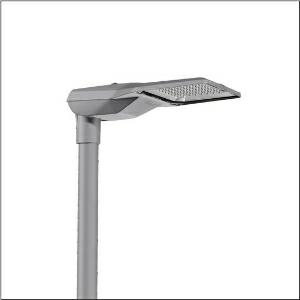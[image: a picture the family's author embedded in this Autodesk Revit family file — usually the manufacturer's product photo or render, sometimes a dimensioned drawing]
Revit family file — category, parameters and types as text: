
# Revit family: streetlight_sl_21_midi___p0_5a_5xe3v33s08nb_fb54
name_source: partatom
category: Lighting Fixtures
units: mm (PartAtom-declared; Revit-internal decimal feet)

## family parameters
Cut with Voids When Loaded = No
Host = Face
Light Source = No
Part Type = Normal
Room Calculation Point = No
Round Connector Dimension = Use Diameter
Shared = No

## types (1)
- --- (1 x LED, 22310 lm, 151.2 W, 3000K)
    Apparent Load = 151 VA
    CIE Flux Codes = 37 73 96 100 100
    Color Rendering = 70
    Color Temperature = 3000K
    Default Elevation = 1800 mm
    Description = Streetlight SL 21 midi, mast luminaire, primary light control with lens, of PMMA, primary optical cover: cover, of toughened safety glass, transparent, light distribution: P0.5a, light emission: direct distribution, primary light characteristic: asymmetric, installation type: post-top, side-entry, LED, High Power LED, rated luminous flux: 22.310lm, luminous efficacy: 148lm/W, light colour: 730, colour temperature: 3000K, control gear: D4i, control: pre-setting: logarithmic dimming characteristic, flexible luminous flux parameterisation, time-dependent luminous flux control, constant luminous flux control, overheat protection, mains connection: 230..240V, AC, 50/60Hz, start of lifetime: 151W, end of service life: 157W, reduction: 70W, luminaire housing, of diecast aluminium, powder-coated, Siteco® metallic grey (DB 702S), corrosivity category C5 mid according to DIN EN ISO 12944, multi-level sealing system, sealing non-destructively replaceable, inclination adjustable: 0°, 5°, 10°, 15°, please order mast flange separately, length: 644mm, width: 335mm, height: 110mm, mast flange for spigot size: 42mm (side-entry): 5XC10008XM4, 60/48mm (side-entry/post-top): 5XC10108XM2, 76/60mm (side-entry/post-top): 5XC10108XM1, mounting height: 4..8m, Smart Interface above, protection rating (complete): IP66, insulation class (complete): insulation class II (safety insulation), certification: CE, ENEC, ENEC+, VDE, impact resistance: IK10, permissible operating ambient temperature for outdoor applications: -40..+50°C, standard-compliant lighting for roads and squares, packaging unit: 1 piece

Light Distribution: P0.5a
    Height = 111 mm
    Lamp = 1 x LED
    Lamp Light Flux = 22310 lm
    Lamp Power = 151.2 W
    Lamp count = 1
    Length = 644 mm
    Luminous efficacy = 148 lm/W
    Manufacturer = Siteco
    ModVariant = No
    Model = 5XE3V33S08NB
    Number of Poles = 1
    OnlyDefault = Yes
    Power Factor = 1
    Product Name = Streetlight SL 21 midi | P0.5a
    Product group = mast luminaire | pylon top
    ProductGroupID = 6100
    Protection Class = Protection class II
    Protection Degree = IP 66
    RLX_Detail_Level = 1
    RLX_Emergency_Light_Flux = 0 lm
    RLX_Emergency_Type = 0
    RLX_Emergency_Type_DB = No
    RlxData = <blob elided: 26653 chars, md5=efacc414>
    Socket = socket
    Standby Power = 0 W
    System Light Flux = 22310 lm
    System Power = 151 W
    Type Comments = factory setting: luminous flux: 100 % | dim-lin: 254 | 802 mA
    Type Image = l_1004302.jpg
    URL = http://relux.com
    VarID = @adj_069042
    Voltage = 0 V
    Weight = 0.00 kg
    Width = 336 mm

## geometry (parser evidence)
native form markers: Blend x4, Sweep x11
no freeform markers — native parametric forms only
